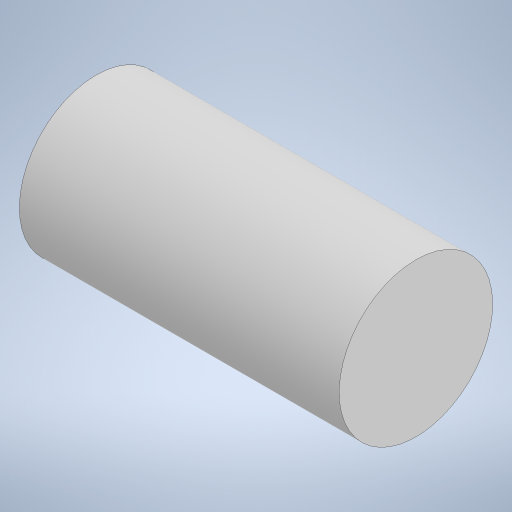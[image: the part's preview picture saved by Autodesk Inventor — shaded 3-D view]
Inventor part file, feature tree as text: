
AUTODESK INVENTOR PART (.ipt)
format: ipt  version: 2023 (Build 270158000, 158)  size: 195,072 bytes
history: native  units: mm
features: extrude x1, sketch x1
ambient origin geometry x8: Origin, YZ Plane, XZ Plane, XY Plane, X Axis, Y Axis, Z Axis, Center Point
bodies: Volumenkörper1 (feature_tree)
feature tree (2):
  extrude  "Extrusion1"  Depth=50.0mm TaperAngle=0.0deg
  sketch  "Skizze1"  dims[d0=24.0mm d1=50.0mm d2=0.0mm]
